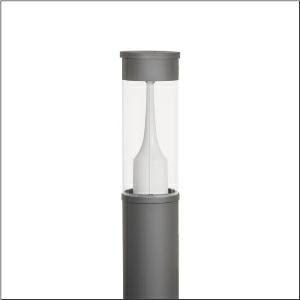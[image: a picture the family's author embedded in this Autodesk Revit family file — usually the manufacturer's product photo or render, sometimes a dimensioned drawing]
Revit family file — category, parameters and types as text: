
# Revit family: city-light_260_iq___st1_2a_5xa5295ef14h_2f06
name_source: partatom
category: Lighting Fixtures
units: mm (PartAtom-declared; Revit-internal decimal feet)

## family parameters
Cut with Voids When Loaded = No
Host = Face
Light Source = No
Part Type = Normal
Room Calculation Point = No
Round Connector Dimension = Use Diameter
Shared = No

## types (1)
- --- (1 x LED, 1540 lm, 10.5 W, 3000K)
    Apparent Load = 11 VA
    CIE Flux Codes = 22 61 93 96 100
    Color Rendering = 70
    Color Temperature = 3000K
    Default Elevation = 1800 mm
    Description = City-Light 260 iQ, light pillar, Module 540 iQ-SR, primary light control with 3 zone facetted reflector, of plastic, silver coated, highly specular, structured, primary optical cover: cover, of PMMA, transparent, light distribution: ST1.2a, primary light characteristic: asymmetric, LED, High Power LED, rated luminous flux: 1.540lm, luminous efficacy: 147lm/W, light colour: 730, colour temperature: 3000K, control gear: ECG iQ, control: Auto-Match, Temp-Guard, Lumen-Switch, Night-Set, Smart-Wire, Light-Fading, Desk-Remote (wireless, voltage-free reading and setting of iQ features in the workshop via application-optimized NFC function/RFID function), optimised constant luminous flux control (CLO 2.0), Street-Remote, presetting dimming logarithmic, with terminal, 6-pole, max. 2.5mm², mains connection: 230..240V, AC, 50/60Hz, start of lifetime: 11W, end of service life: 11W, reduction: 5W, luminaire housing, cylindrical, of extruded aluminium section, coated, Siteco® metallic grey (DB 702S), length: 2.600mm, diameter: 200mm, Module 540 iQ-SR, traffic white (RAL 9016), equipment: standard, protection rating (complete): IP65, insulation class (complete): insulation class II (safety insulation), certification: CE, ENEC, VDE, packaging unit: 1 piece

Light Distribution: ST1.2a
    Height = 500 mm
    Lamp = 1 x LED
    Lamp Light Flux = 1540 lm
    Lamp Power = 10.5 W
    Lamp count = 1
    Length = 200 mm
    Luminous efficacy = 147 lm/W
    Manufacturer = Siteco
    ModVariant = No
    Model = 5XA5295EF14H
    Mounting Place = Floor
    Mounting Type = Freestanding
    Number of Poles = 1
    OnlyDefault = Yes
    Power Factor = 1
    Product Name = City-Light 260 iQ | ST1.2a
    Product group = light pillar
    ProductGroupID = 1303
    Protection Class = Protection class II
    Protection Degree = IP 65
    RLX_Detail_Level = 1
    RLX_Emergency_Light_Flux = 0 lm
    RLX_Emergency_Type = 0
    RLX_Emergency_Type_DB = No
    RlxData = <blob elided: 60657 chars, md5=a50a0420>
    Socket = socket
    Standby Power = 0 W
    System Light Flux = 1540 lm
    System Power = 11 W
    Type Comments = factory setting: luminous flux: 100 % | dim-lin: 254 | 419 mA
    Type Image = l_1006918.jpg
    URL = http://relux.com
    VarID = @adj_109379
    Voltage = 0 V
    Weight = 0.00 kg
    Width = 0 mm  [stored 0 ft]

note: [stored X ft] marks values corroborated as IEEE doubles in the binary element streams (Revit-internal decimal feet)

## geometry (parser evidence)
native form markers: Blend x4, Sweep x11
no freeform markers — native parametric forms only
